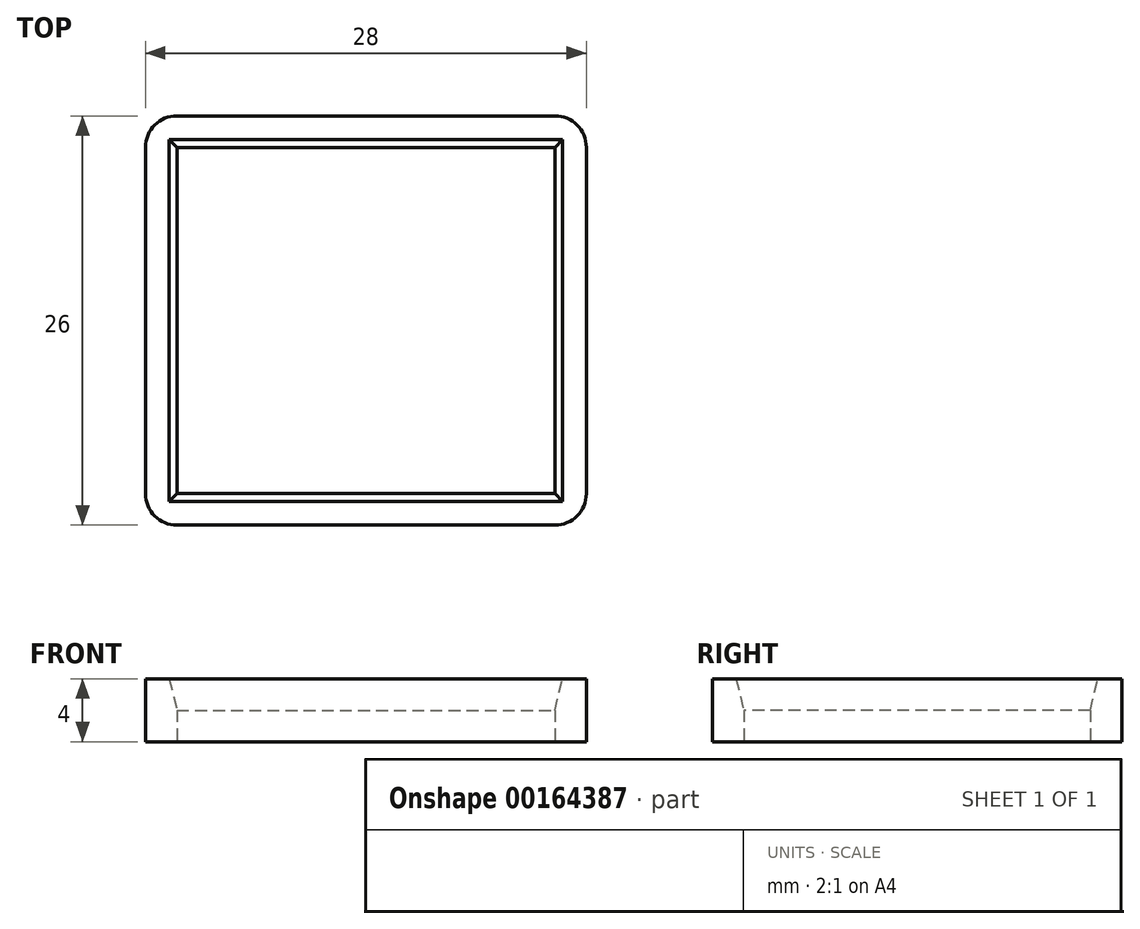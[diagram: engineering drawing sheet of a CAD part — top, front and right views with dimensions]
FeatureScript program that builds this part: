
annotation { "Feature Type Name" : "Feature", "Feature Type Description" : "" }
export const myFeature = defineFeature(function(context is Context, id is Id, definition is map)
    precondition{}
    {
        {
            var Q0;
            Q0=qCreatedBy(makeId("Top.planeOp"),FACE);
            var sketch = newSketch(context, id + "F0", { "sketchPlane" : qUnion([Q0])});
            skLineSegment(sketch, "E0.bottom", {"start": v(-14, 13) * mm, "end": v(-12, 13) * mm});
            skLineSegment(sketch, "E0.top", {"start": v(-14, -13) * mm, "end": v(-12, -13) * mm});
            skLineSegment(sketch, "E0.left", {"start": v(-14, 13) * mm, "end": v(-14, -13) * mm});
            skLineSegment(sketch, "E0.right", {"start": v(-12, 13) * mm, "end": v(-12, -13) * mm});
            skLineSegment(sketch, "E1.bottom", {"start": v(-12, 13) * mm, "end": v(12, 13) * mm});
            skLineSegment(sketch, "E1.top", {"start": v(-12, 11) * mm, "end": v(12, 11) * mm});
            skLineSegment(sketch, "E1.left", {"start": v(-12, 13) * mm, "end": v(-12, 11) * mm});
            skLineSegment(sketch, "E1.right", {"start": v(12, 13) * mm, "end": v(12, 11) * mm});
            skLineSegment(sketch, "E2.bottom", {"start": v(-12, -13) * mm, "end": v(12, -13) * mm});
            skLineSegment(sketch, "E2.top", {"start": v(-12, -11) * mm, "end": v(12, -11) * mm});
            skLineSegment(sketch, "E2.left", {"start": v(-12, -13) * mm, "end": v(-12, -11) * mm});
            skLineSegment(sketch, "E2.right", {"start": v(12, -13) * mm, "end": v(12, -11) * mm});
            skLineSegment(sketch, "E3.bottom", {"start": v(12, 13) * mm, "end": v(14, 13) * mm});
            skLineSegment(sketch, "E3.top", {"start": v(12, -13) * mm, "end": v(14, -13) * mm});
            skLineSegment(sketch, "E3.left", {"start": v(12, 13) * mm, "end": v(12, -13) * mm});
            skLineSegment(sketch, "E3.right", {"start": v(14, 13) * mm, "end": v(14, -13) * mm});
            skSolve(sketch);
        }
        {
            var Q0;
            Q0 = qSketchRegion(id + "F0", true);
            extrude(context, id + "F1", {"entities" : qUnion([Q0]), "depth" : 4 * mm});
        }
        {
            var Q0;
            Q0=makeQuery(id+"F1.opExtrude","CAP_EDGE",EDGE,{"disambiguationData":[OSD([sQuery(id+"F0.wireOp",EDGE,"E0.right")])],"isStart":false});
            var Q1;
            Q1=makeQuery(id+"F1.opExtrude","CAP_EDGE",EDGE,{"disambiguationData":[OSD([sQuery(id+"F0.wireOp",EDGE,"E1.top")])],"isStart":false});
            var Q2;
            Q2=makeQuery(id+"F1.opExtrude","CAP_EDGE",EDGE,{"disambiguationData":[OSD([sQuery(id+"F0.wireOp",EDGE,"E3.left")])],"isStart":false});
            var Q3;
            Q3=makeQuery(id+"F1.opExtrude","CAP_EDGE",EDGE,{"disambiguationData":[OSD([sQuery(id+"F0.wireOp",EDGE,"E2.top")])],"isStart":false});
            chamfer(context, id + "F2", {"entities" : qUnion([Q0, Q1, Q2, Q3]), "chamferType" : ChamferType.TWO_OFFSETS, "width1" : 0.5 * mm, "oppositeDirection" : true, "width2" : 2 * mm, "tangentPropagation" : true});
        }
        {
            var Q0;
            Q0=makeQuery(id+"F1.opExtrude","SWEPT_EDGE",EDGE,{"disambiguationData":[OSD([sQuery(id+"F0.wireOp",EDGE,"E3.top"),sQuery(id+"F0.wireOp",EDGE,"E3.right")])]});
            var Q1;
            Q1=makeQuery(id+"F1.opExtrude","SWEPT_EDGE",EDGE,{"disambiguationData":[OSD([sQuery(id+"F0.wireOp",EDGE,"E0.top"),sQuery(id+"F0.wireOp",EDGE,"E0.left")])]});
            var Q2;
            Q2=makeQuery(id+"F1.opExtrude","SWEPT_EDGE",EDGE,{"disambiguationData":[OSD([sQuery(id+"F0.wireOp",EDGE,"E0.bottom"),sQuery(id+"F0.wireOp",EDGE,"E0.left")])]});
            var Q3;
            Q3=makeQuery(id+"F1.opExtrude","SWEPT_EDGE",EDGE,{"disambiguationData":[OSD([sQuery(id+"F0.wireOp",EDGE,"E3.bottom"),sQuery(id+"F0.wireOp",EDGE,"E3.right")])]});
            fillet(context, id + "F3", {"entities" : qUnion([Q0, Q1, Q2, Q3]), "radius" : 2 * mm, "tangentPropagation" : true, "allowEdgeOverflow" : false});
        }
    });
